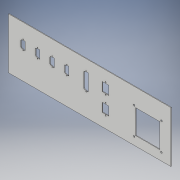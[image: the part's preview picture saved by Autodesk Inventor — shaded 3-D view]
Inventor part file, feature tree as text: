
AUTODESK INVENTOR PART (.ipt)
format: ipt  version: 2017 (Build 210142000, 142)  size: 289,280 bytes
history: native  units: in
note: dims shown in document units (in); Inventor stores cm internally (conversion verified against a paired STEP export)
features: extrude x5, hole x4, other x3, sketch x3
ambient origin geometry x8: Origin, YZ Plane, XZ Plane, XY Plane, X Axis, Y Axis, Z Axis, Center Point
bodies: Solid1 (feature_tree)
feature tree (15):
  extrude  "pdu"  Depth=5.256in
  other  "dsub9 sketch"
  other  "dsub25 sketch"
  other  "CAT7 sketch"
  hole  "airflow holes"  [1 undecoded]
  extrude  "airflow cutout"  Depth=2.5in
  hole  "dsub9 4-40 holes"  [1 undecoded]
  extrude  "dsub9 cutouts"  Depth=2.5in
  hole  "CAT7 holes"  [1 undecoded]
  extrude  "CAT7 cutout"  Depth=2.5in
  hole  "dsub25 4-40 holes"  [1 undecoded]
  extrude  "dsub25 cutout"  Depth=2.5in
  sketch  "Sketch1"  dims[d0=16.73in d1=5.256in]
  sketch  "Sketch5"  dims[d2=0.065in d3=0.0in d4=0.089in]
  sketch  "Sketch7"  dims[d5=0.089in d6=0.984in d7=0.166in d8=0.166in d9=0.166in d10=0.166in d11=0.583in d12=0.708in d13=0.325in d14=0.325in d15=0.12in d16=0.12in d17=1.5in d18=0.23in d19=0.46in d20=2.75in d21=0.2952in d22=1.5748in d24=1.5in d25=0.3937in d27=1.0in d31=0.089in d32=0.089in d33=1.852in d34=0.166in d35=0.166in d36=0.166in d37=0.166in d38=1.452in d39=1.577in d40=2.0in d41=0.46in d42=0.23in d43=8.0in d44=2.319in d47=0.9in d48=0.675in d49=0.089in d50=0.089in d51=1.142in d52=3.029in d53=10.0in d54=0.7874in d56=1.852in d57=0.3937in d59=1.0in d63=3.3in d64=3.3in d65=12.7in d66=0.535in d67=2.5in d68=2.5in d69=2.81in d70=0.177in d71=0.177in d72=0.177in d73=0.177in d76=0.177in d77=0.75in d78=0.332in d79=0.25in d80=0.5635in d81=1.0in d82=0.8108in d83=3.3in d84=3.3in d85=12.7in d86=0.535in d87=2.5in d88=2.5in d89=2.81in d90=0.177in d91=0.177in d92=0.177in d93=0.177in d94=0.0in d95=0.0in d96=0.085in d97=0.224in d98=0.375in d99=0.25in d100=0.5635in d101=0.349in d102=0.8108in d103=0.0in d104=0.0in d105=0.116in d106=0.224in d107=0.375in d108=0.25in d109=0.5635in d110=0.349in d111=0.8108in d112=0.0in d113=0.0in d114=0.085in d115=0.224in d116=0.375in d117=0.25in d118=0.5635in d119=0.349in d120=0.8108in d121=0.0in d122=0.0in]
note: 4 required parameter values undecoded (feature->parameter linkage not recoverable at this tier; creation-order binding heuristic only, values carry confidence <= 0.55)
